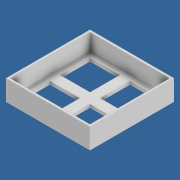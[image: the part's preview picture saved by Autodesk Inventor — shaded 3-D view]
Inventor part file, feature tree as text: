
AUTODESK INVENTOR PART (.ipt)
format: ipt  version: 2020 (Build 240168000, 168)  size: 143,360 bytes
history: native  units: in
note: dims shown in document units (in); Inventor stores cm internally (conversion verified against a paired STEP export)
features: extrude x3, sketch x3
ambient origin geometry x8: Origin, YZ Plane, XZ Plane, XY Plane, X Axis, Y Axis, Z Axis, Center Point
bodies: Solid1 (feature_tree)
feature tree (6):
  extrude  "Extrusion1"  Depth=1.626in
  extrude  "Extrusion7"  Depth=1.5472in
  extrude  "Extrusion8"  Depth=0.0394in
  sketch  "Sketch1"  dims[d0=1.626in d1=1.626in]
  sketch  "Sketch8"  dims[d2=0.3937in d3=0.0in d61=1.5472in]
  sketch  "Sketch9"  dims[d62=1.5472in d63=0.0394in d64=0.0394in d65=0.3346in d66=0.0in d67=0.5787in d68=0.5787in d69=0.0965in d70=0.0965in d71=0.5787in d72=0.5787in d73=0.1969in d74=0.5787in d75=0.5787in d76=0.1969in d77=0.0965in d78=0.5787in d79=0.5787in d80=0.1969in d81=0.1969in d82=0.3346in d83=0.0in]
